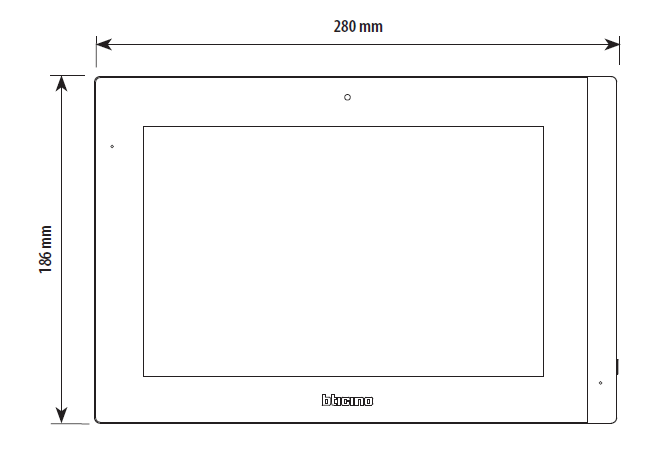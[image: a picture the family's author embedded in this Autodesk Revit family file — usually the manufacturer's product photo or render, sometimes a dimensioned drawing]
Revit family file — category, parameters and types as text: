
# Revit family: Bticino-Portier-Classe 300EOS-Poste Intérieur
name_source: partatom
category: Equipement électrique
units: mm (PartAtom-declared; Revit-internal decimal feet)

## family parameters
Configuration du panneau = Deux colonnes, circuits au sein
Cote de connecteur circulaire = Utiliser le diamètre
Couper avec des vides une fois chargée = Non
Hôte = Face
Partagée = Non
Point de calcul de pièce = Non
Type d'élément = Tableau de raccordement

## types (2) — shared parameters
Avec video = Oui
Bouton ouverture porte = Oui
Camera = Sans Caméra
Conditions Générale d'Utilisation = https://export.legrand.com
Couleur = Blanc
Ecran Tactile = Oui
Elévation par défaut = 1100 mm
Hauteur = 222 mm
IP = 54
L3 = 115 mm  [stored 0.377297 ft]
Largeur = 121 mm  [stored 0.396982 ft]
Mode de pose = saillie
Objet Connecté = Oui
Profondeur = 32 mm  [stored 0.104987 ft]
Résolution écran = 1280x720
Site web configurateur = https://www.homesystems-legrandgroup.com
Taille de l'écran (Pouces) = 5
Temperature d'utilisation MIN-MAX = +5/+40 °C
Tension = 20-27 V DC
Type d'interface = Wi-Fi/ RJ45
Type de raccordement = système bus

## per-type parameters (varying)
| type | Compatible avec appareil de correction auditive | Référence / Modèle | Teleloop |
| CLASSE 300EOS WITH NETATMO (Alexa intégré) | Non | BT-344842 | Non |
| POSTE INTERIEUR CLASSE 300EOS WITH NETATMO BOUCLE Inductive (Alexa intégré) | Oui | BT-344845 | Oui |

note: column(s) folded — value = type name in every type: Désignation produit

note: [stored X ft] marks values corroborated as IEEE doubles in the binary element streams (Revit-internal decimal feet)
